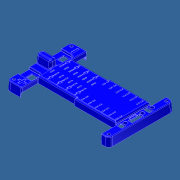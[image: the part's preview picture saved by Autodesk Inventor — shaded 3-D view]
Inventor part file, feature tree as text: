
AUTODESK INVENTOR PART (.ipt)
format: ipt  version: 2012 (Build 160160000, 160)  size: 5,834,752 bytes
history: native  units: mm (DEFAULTED — no unit token found)
features: extrude x32, sketch x27, fillet x20, other x10, pattern_linear x3, plane x3, projected_geometry x2, pattern_circular x1
ambient origin geometry x5: Origin, X Axis, Y Axis, Z Axis, Center Point
bodies: Solid1 (feature_tree)
feature tree (98):
  other  "Main Body Sketch"
  other  "Primary Mounting Hole Axis"
  extrude  "Above the PCB Extrusion"  Depth=9.652mm
  extrude  "Below Extrusion"  Depth=217.0mm
  extrude  "Mounting Holes"  Depth=6.5278mm
  extrude  "Wago Holes"  Depth=209.55mm
  extrude  "Upper Level Boss"  Depth=142.875mm
  other  "Upper Level Bevel"
  other  "LED Sketch"
  extrude  "LED Holes"  Depth=2.54mm
  extrude  "LED Hole Up"  Depth=29.21mm
  extrude  "Lug Recesses"  Depth=2.54mm
  extrude  "Anti-Wrench Bump"  Depth=1.397mm
  fillet  "Pre Shell Fillet 1"  Radius=0.508mm
  extrude  "Mounting Hole Rib"  Depth=2.54mm
  other  "Mounting Hole Rib Draft"
  extrude  "Wago Hole Clearing"  Depth=15.0mm
  extrude  "Lug Holes"  Depth=10.0mm
  extrude  "Big CB Hole"  Depth=90.0mm
  extrude  "Big CB Holder Relief"  Depth=0.836185mm
  fillet  "Big CB Fillet 1"  Radius=2.159mm
  fillet  "Big CB Fillet 2"  Radius=1.7018mm
  pattern_linear  "Big CB Hole Pattern"  Count1=9  [1 undecoded]
  extrude  "Medium CB Holes"  Depth=0.508mm
  fillet  "Medium CB Fillet 1"  Radius=14.0mm
  fillet  "Medium CB Fillet 2"  Radius=1.6mm
  pattern_linear  "Medium CB Hole Pattern"  Count1=5  [1 undecoded]
  other  "Connector Holes"
  extrude  "Small Wago Holes"  Depth=2.54mm
  extrude  "cRio Connector Hole"  Depth=0.174533mm
  extrude  "cRio Connector Hole Clearance"  Depth=0.381mm
  extrude  "LED Hole Clearing"  Depth=13.762mm
  extrude  "Bottom Recess Cut"  Depth=29.1846mm
  extrude  "Side Cutouts for Bottom to Fill"  Depth=32.2834mm
  extrude  "Side Cutouts Extension"  Depth=0.254mm
  extrude  "Screw Bosses"  Depth=0.254mm
  other  "Ribs 1"
  extrude  "Main Rib"  Depth=0.254mm
  extrude  "Main Rib Component Cuts"  Depth=0.254mm
  extrude  "PS LED Rib"  Depth=15.0mm
  extrude  "Medium CB Holder Clearance Cuts"  Depth=70.0mm
  extrude  "Medium CB Area Ribs"  Depth=7.62mm
  other  "Bottom Support Ribs"
  extrude  "Battery Polarity Indicator Emboss"  Depth=7.62mm
  extrude  "LED FET Notch"  Depth=2.032mm TaperAngle=0.0deg
  other  "CB Indicator Sketch"
  extrude  "CB Indicator"  TaperAngle=0.0deg  [1 undecoded]
  fillet  "CB Indicator Fillet"  [1 undecoded]
  pattern_linear  "CB Indicator Pattern"  Spacing1=15.0deg  [1 undecoded]
  other  "CB Indicator Flip Axis"
  pattern_circular  "CB Indicator Flip"  [2 undecoded]
  fillet  "Through Hole Corner Fillets"  Radius=13.97mm
  fillet  "Top Fillets 1"  Radius=8.726646mm
  fillet  "Top Fillets 2"  Radius=0.349066mm
  fillet  "Top Fillets 3"  Radius=0.349066mm
  extrude  "Fillet Fill In / Undercut Prevention"  Depth=38.1mm
  fillet  "Bottom Fillets 1"  Radius=27.94mm
  fillet  "Bottom Intersection Fillets 1"  Radius=85.08mm
  fillet  "Mounting Hole, Bottom Recess Fillets"  Radius=5.207mm
  fillet  "Bottom Fillets 2"  Radius=34.7726mm
  fillet  "Rib Intersection Fillets"  Radius=2.032mm
  fillet  "Other Intersection Fillets"  Radius=2.032mm
  fillet  "Rib Edge Fillets"  Radius=0.523599mm
  fillet  "Through Hole Edge Fillets"  Radius=25.9842mm
  fillet  "Final Fillets 1"  Radius=99.70017mm
  fillet  "Final Fillets 2"  Radius=0.79375mm
  plane  "YZ Plane (RIGHT)"
  plane  "XZ Plane (TOP)"
  plane  "XY Plane (FRONT)"
  sketch  "Sketch7"  dims[d2=9.398mm d3=-0.523599mm d4=9.652mm d5=0.523599mm]
  sketch  "Sketch8"  dims[d6=2.54mm d12=217.0mm]
  sketch  "Sketch9"  dims[d13=135.1788mm d14=6.5278mm]
  sketch  "Sketch10"  dims[d15=127.0mm d16=209.55mm]
  sketch  "Sketch11"  dims[d19=225.425mm d20=142.875mm]
  sketch  "Sketch16"  dims[d21=7.9375mm d22=1.27mm d28=2.54mm d29=-0.349066mm]
  sketch  "Sketch17"  dims[d31=0.508mm d32=29.21mm]
  sketch  "Sketch21"  dims[d33=1.397mm d35=2.54mm d36=0.349066mm]
  sketch  "Sketch23"  dims[d37=80.0mm d39=10.0mm d41=1.397mm d42=0.508mm]
  sketch  "Sketch24"  dims[d43=13.843mm d44=2.54mm d45=0.349066mm]
  sketch  "Sketch25"  dims[d49=5.7023mm d50=15.0mm]
  sketch  "Sketch26"  dims[d51=60.0mm d53=15.0mm d54=10.0mm]
  sketch  "Sketch30"  dims[d55=81.7mm d56=90.0mm]
  sketch  "Sketch31"  dims[d57=28.8036mm d58=0.836185mm d61=2.159mm d64=1.7018mm]
  sketch  "Sketch32"  dims[d65=0.836185mm]
  sketch  "Sketch33"  dims[d68=1.7mm d71=90.0mm]
  sketch  "Sketch34"  dims[d72=2.059mm d73=0.508mm d74=14.0mm d76=1.6mm d77=50.0mm]
  sketch  "Sketch35"  dims[d78=1.0922mm d80=2.54mm d81=0.349066mm]
  sketch  "Sketch36"  dims[d84=2.54mm d85=0.349066mm d88=0.174533mm]
  projected_geometry  "Projected Loop2"
  projected_geometry  "Projected Loop3"
  sketch  "Sketch38"  dims[d90=90.0deg d91=0.381mm d92=-2.617994mm]
  sketch  "Sketch40"  dims[d93=13.762mm d94=13.762mm]
  sketch  "Sketch41"  dims[d95=32.2834mm d96=29.1846mm]
  sketch  "Sketch42"  dims[d98=21.0mm d102=32.2834mm]
  sketch  "Sketch43"  dims[d104=29.1846mm d110=0.254mm]
  sketch  "Sketch44"  dims[d112=0.254mm d113=0.254mm]
  sketch  "Sketch45"  dims[d114=25.4mm d115=-0.523599mm d116=0.254mm]
  sketch  "Sketch46"  dims[d117=0.254mm d118=0.254mm d119=15.0mm d121=70.0mm d122=7.62mm d123=7.62mm d124=2.032mm d125=1.524mm d127=0.0mm d128=0.0mm d129=15.0deg d130=15.0deg d131=1.524mm d132=13.97mm d135=8.726646mm d138=0.349066mm d139=0.349066mm d140=38.1mm d141=27.94mm d142=85.08mm d143=5.207mm d144=-0.349066mm d145=34.7726mm d147=2.032mm d148=2.032mm d155=0.523599mm d156=25.9842mm d157=99.70017mm d158=0.79375mm d159=0.508mm d160=9.398mm d161=8.509mm d163=4.9mm d164=7.62mm d165=0.349066mm d167=0.508mm d169=10.414mm d176=5.08mm d177=-2.617994mm d178=7.0mm d180=5.08mm d181=0.349066mm d182=15.0deg d183=5.08mm d184=4.0mm d185=1.869182mm d200=0.396875mm d201=0.396875mm d202=0.396875mm d203=0.396875mm d204=20.0mm d205=40.0mm d207=20.0mm d208=20.0mm d209=360.0deg d211=7.62mm d212=10.922mm d213=1.27mm d214=-0.349066mm d215=0.508mm d216=0.508mm d217=21.1mm d218=2.54mm d219=1.27mm d220=-0.349066mm d221=1.524mm d222=1.524mm d223=1.016mm d224=1.27mm d225=2.794mm d226=-0.349066mm d227=1.27mm d228=1.27mm d229=1.27mm d230=2.794mm d231=0.174533mm d232=3.6068mm d233=1.524mm d234=0.0mm d235=120.0mm d236=55.0mm d237=44.5mm d238=10.0mm d239=172.0mm d240=95.0mm d241=189.0mm d242=40.0mm d252=1.524mm d253=7.62mm d254=15.24mm d255=19.05mm d256=-0.523599mm d257=0.728441mm d258=3.81mm d262=0.396875mm d263=0.396875mm d264=0.396875mm d265=20.0mm d266=0.396875mm d267=0.396875mm d268=0.396875mm d269=0.79375mm d270=0.396875mm d277=1.397mm d278=2.54mm d279=0.174533mm d280=1.397mm d281=25.4mm d282=0.174533mm d284=0.523599mm d285=25.4mm d286=0.0mm d287=78.128mm d288=0.523599mm d289=5.588mm d293=110.236mm d294=91.2876mm d295=4.064mm d296=0.79375mm d298=0.254mm d299=0.396875mm d300=6.6548mm d302=1.524mm d303=13.962634mm d304=1.016mm d305=0.396875mm d306=0.79375mm d315=2.794mm d317=0.79375mm d318=0.508mm d319=2.794mm d320=1.27mm d321=0.79375mm d322=1.27mm d325=0.396875mm d326=7.239mm d328=7.8232mm d329=-0.349066mm d331=1.524mm d332=15.0mm d333=70.0mm d334=12.7mm d337=4.572mm d338=-0.523599mm d339=0.79375mm d340=25.4mm d341=1.22173mm d343=0.127mm d344=1.778mm d346=25.4mm d347=6.35mm d348=19.05mm d349=80.264mm d350=165.631mm d351=3.81mm d352=15.24mm d353=58.42mm d354=3.81mm d355=15.24mm d356=58.42mm d357=92.075mm d358=0.396875mm d360=0.396875mm d361=0.381mm d362=-2.617994mm d363=0.396875mm d364=0.127mm d365=1.27mm d366=1.27mm d367=1.27mm d368=1.27mm d372=0.635mm d373=25.4mm d374=-0.349066mm d375=0.635mm d377=0.635mm d378=0.635mm d379=0.254mm d380=0.127mm d382=33.5mm d383=6.35mm d384=0.508mm d385=1.778mm d386=0.508mm d387=0.6096mm d388=7.239mm d389=24.3078mm d390=0.5mm d391=0.25mm d393=13.4mm d395=8.5mm d396=0.508mm d397=15.0114mm d399=1.0668mm d400=-0.349066mm d401=1.0668mm d402=-0.349066mm d403=3.81mm d404=0.508mm d406=1.0668mm d407=0.523599mm d409=1.905mm d410=8.509mm d411=13.3096mm d412=14.0mm d413=35.7mm d414=23.5mm d415=7.0mm d416=7.0mm d417=26.1mm d418=3.5mm d419=0.088699mm d420=0.088699mm d421=4.363323mm d422=0.508mm d423=3.0mm d424=1.4mm d425=0.381mm d426=0.381mm d428=35.9305mm d429=32.0mm d430=1.27mm d431=-0.349066mm d434=0.396875mm d435=135.651mm d436=151.131mm d437=1.524mm d438=1.524mm d439=1.016mm d440=0.174533mm d441=1.592078mm d442=1.592078mm d443=1.592078mm d444=1.016mm d445=0.174533mm d446=1.778mm d447=1.592078mm d450=2.286mm d451=0.396875mm d452=2.286mm d453=1.016mm d454=0.396875mm d455=0.79375mm d456=0.396875mm d457=0.396875mm d458=0.396875mm d459=1.524mm d460=45.0deg d461=1.524mm d462=45.0deg d463=45.0deg d464=2.032mm d465=2.54mm d466=0.174533mm d467=0.254mm d472=25.4mm d473=0.349066mm d474=0.127mm d475=0.254mm d476=0.127mm d477=0.396875mm d478=0.254mm d479=0.79375mm d480=0.127mm d481=0.79375mm d484=7.62mm d485=0.632986mm d486=0.836185mm]
note: 7 required parameter values undecoded (feature->parameter linkage not recoverable at this tier; creation-order binding heuristic only, values carry confidence <= 0.55)
